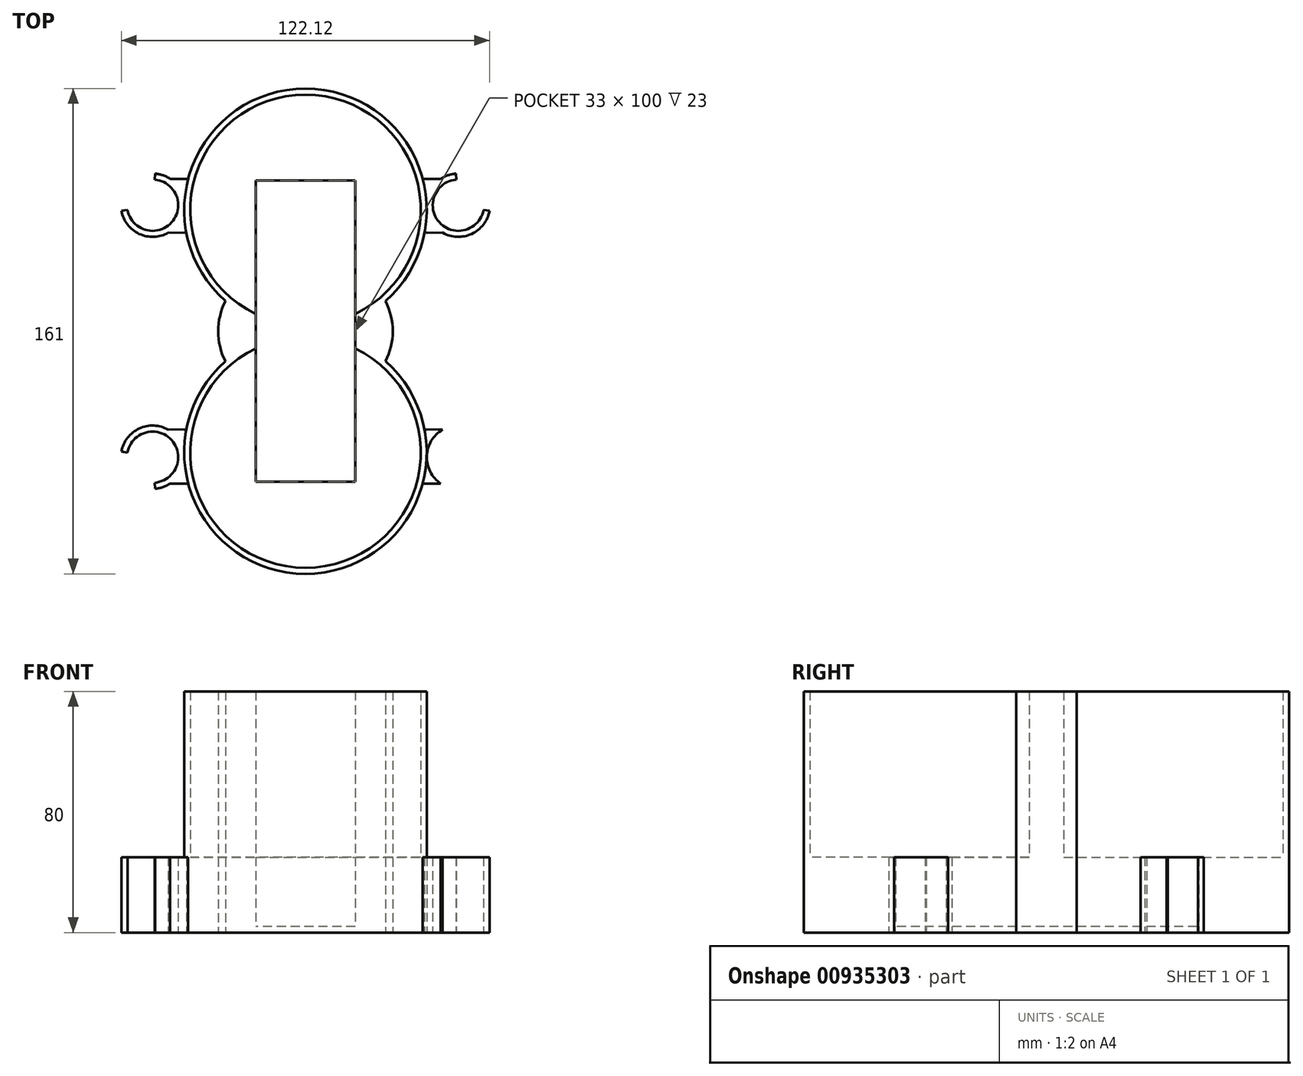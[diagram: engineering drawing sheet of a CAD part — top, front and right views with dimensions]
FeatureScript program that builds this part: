
annotation { "Feature Type Name" : "Feature", "Feature Type Description" : "" }
export const myFeature = defineFeature(function(context is Context, id is Id, definition is map)
    precondition{}
    {
        {
            var Q0;
            Q0=qCreatedBy(makeId("Top.planeOp"),FACE);
            var sketch = newSketch(context, id + "F0", { "sketchPlane" : qUnion([Q0])});
            skCircle(sketch, "E0", {"center": v(0, 40.25) * mm, "radius": 38.25 * mm});
            skCircle(sketch, "E1.0", {"center": v(0, 40.25) * mm, "radius": 40.25 * mm});
            skCircle(sketch, "E2", {"center": v(0, -40.25) * mm, "radius": 38.25 * mm});
            skCircle(sketch, "E3.0", {"center": v(0, -40.25) * mm, "radius": 40.25 * mm});
            skLineSegment(sketch, "E4", {"start": v(0, 0) * mm, "end": v(0, 0) * mm});
            skLineSegment(sketch, "E5", {"start": v(19.43, 5) * mm, "end": v(19.43, -5) * mm});
            skLineSegment(sketch, "E6.bottom", {"start": v(16.5, 50) * mm, "end": v(-16.5, 50) * mm});
            skLineSegment(sketch, "E6.top", {"start": v(16.5, -50) * mm, "end": v(-16.5, -50) * mm});
            skLineSegment(sketch, "E6.left", {"start": v(16.5, 50) * mm, "end": v(16.5, -50) * mm});
            skLineSegment(sketch, "E6.right", {"start": v(-16.5, 50) * mm, "end": v(-16.5, -50) * mm});
            skPoint(sketch, "E6.middle", {"position": v(0, 0) * mm});
            skArc(sketch, "E7", {"start": v(26.55, -10) * mm, "mid": v(28.96, 0) * mm, "end": v(26.55, 10) * mm});
            skArc(sketch, "E8.MirrorCS", {"start": v(-26.55, -10) * mm, "mid": v(-28.96, 0) * mm, "end": v(-26.55, 10) * mm});
            skLineSegment(sketch, "E9.MirrorCS", {"start": v(-19.43, 5) * mm, "end": v(-19.43, -5) * mm});
            skSolve(sketch);
        }
        {
            var Q0;
            Q0 = qSketchRegion(id + "F0", true);
            var Q1;
            {var subQ0=sQuery(id+"F0.wireOp",EDGE,"E5");Q1=makeQuery(id+"F0.imprint","IMPRINT",FACE,{"disambiguationData":[TD([[makeQuery(id+"F0.imprint","IMPRINT",EDGE,{"derivedFrom":subQ0}),-1.0]])]});}
            var Q2;
            {var subQ0=sQuery(id+"F0.wireOp",EDGE,"E9.MirrorCS");Q2=makeQuery(id+"F0.imprint","IMPRINT",FACE,{"disambiguationData":[TD([[makeQuery(id+"F0.imprint","IMPRINT",EDGE,{"derivedFrom":subQ0}),1.0]])]});}
            extrude(context, id + "F1", {"entities" : qUnion([Q0, Q1, Q2]), "depth" : 80 * mm, "offsetDistance" : 25 * mm});
        }
        {
            var Q0;
            {var subQ5=sQuery(id+"F0.wireOp",EDGE,"E6.top");Q0=makeQuery(id+"F0.imprint","IMPRINT",FACE,{"disambiguationData":[TD([[makeQuery(id+"F0.imprint","IMPRINT",EDGE,{"derivedFrom":subQ5}),1.0]])]});}
            var Q1;
            {var subQ5=sQuery(id+"F0.wireOp",EDGE,"E6.bottom");Q1=makeQuery(id+"F0.imprint","IMPRINT",FACE,{"disambiguationData":[TD([[makeQuery(id+"F0.imprint","IMPRINT",EDGE,{"derivedFrom":subQ5}),-1.0]])]});}
            var Q2;
            {var subQ5=sQuery(id+"F0.wireOp",EDGE,"E6.top");Q2=makeQuery(id+"F0.imprint","IMPRINT",FACE,{"disambiguationData":[TD([[makeQuery(id+"F0.imprint","IMPRINT",EDGE,{"derivedFrom":subQ5}),-1.0]])]});}
            var Q3;
            {var subQ5=sQuery(id+"F0.wireOp",EDGE,"E6.bottom");Q3=makeQuery(id+"F0.imprint","IMPRINT",FACE,{"disambiguationData":[TD([[makeQuery(id+"F0.imprint","IMPRINT",EDGE,{"derivedFrom":subQ5}),1.0]])]});}
            var Q4;
            {var subQ0=sQuery(id+"F0.wireOp",EDGE,"E5");Q4=makeQuery(id+"F0.imprint","IMPRINT",FACE,{"disambiguationData":[TD([[makeQuery(id+"F0.imprint","IMPRINT",EDGE,{"derivedFrom":subQ0}),-1.0]])]});}
            var Q5;
            {var subQ0=sQuery(id+"F0.wireOp",EDGE,"E9.MirrorCS");Q5=makeQuery(id+"F0.imprint","IMPRINT",FACE,{"disambiguationData":[TD([[makeQuery(id+"F0.imprint","IMPRINT",EDGE,{"derivedFrom":subQ0}),1.0]])]});}
            var Q6;
            {var subQ0=sQuery(id+"F0.wireOp",EDGE,"E6.right");var subQ1=sQuery(id+"F0.wireOp",EDGE,"E1.0");var subQ2=makeQuery(id+"F0.imprint","INTERSECT",VERTEX,{"derivedFrom":[subQ1,subQ0]});Q6=makeQuery(id+"F0.imprint","IMPRINT",FACE,{"disambiguationData":[TD([[makeQuery(id+"F0.imprint","IMPRINT",EDGE,{"disambiguationData":[TD([[subQ2,-1.0]])],"derivedFrom":subQ1}),-1.0]])]});}
            var Q7;
            {var subQ0=sQuery(id+"F0.wireOp",EDGE,"E6.left");var subQ1=sQuery(id+"F0.wireOp",EDGE,"E0");var subQ2=makeQuery(id+"F0.imprint","INTERSECT",VERTEX,{"derivedFrom":[subQ1,subQ0]});Q7=makeQuery(id+"F0.imprint","IMPRINT",FACE,{"disambiguationData":[TD([[makeQuery(id+"F0.imprint","IMPRINT",EDGE,{"disambiguationData":[TD([[subQ2,1.0]])],"derivedFrom":subQ1}),-1.0]])]});}
            var Q8;
            {var subQ2=sQuery(id+"F0.wireOp",EDGE,"E6.left");var subQ4=sQuery(id+"F0.wireOp",EDGE,"E2");var subQ5=makeQuery(id+"F0.imprint","INTERSECT",VERTEX,{"derivedFrom":[subQ4,subQ2]});Q8=makeQuery(id+"F0.imprint","IMPRINT",FACE,{"disambiguationData":[TD([[makeQuery(id+"F0.imprint","IMPRINT",EDGE,{"disambiguationData":[TD([[subQ5,-1.0]])],"derivedFrom":subQ4}),-1.0]])]});}
            var Q9;
            {var subQ0=sQuery(id+"F0.wireOp",EDGE,"E3.0");var subQ1=sQuery(id+"F0.wireOp",EDGE,"E1.0");var subQ2=makeQuery(id+"F0.imprint","INTERSECT",VERTEX,{"derivedFrom":[subQ1,subQ0]});Q9=makeQuery(id+"F0.imprint","IMPRINT",FACE,{"disambiguationData":[TD([[makeQuery(id+"F0.imprint","IMPRINT",EDGE,{"disambiguationData":[TD([[subQ2,-1.0]])],"derivedFrom":subQ1}),-1.0]])]});}
            extrude(context, id + "F2", {"entities" : qUnion([Q0, Q1, Q2, Q3, Q4, Q5, Q6, Q7, Q8, Q9]), "operationType" : NewBodyOperationType.ADD, "depth" : 25 * mm, "offsetDistance" : 25 * mm});
        }
        {
            var Q0;
            {var subQ5=sQuery(id+"F0.wireOp",EDGE,"E6.bottom");Q0=makeQuery(id+"F0.imprint","IMPRINT",FACE,{"disambiguationData":[TD([[makeQuery(id+"F0.imprint","IMPRINT",EDGE,{"derivedFrom":subQ5}),1.0]])]});}
            var Q1;
            {var subQ5=sQuery(id+"F0.wireOp",EDGE,"E6.top");Q1=makeQuery(id+"F0.imprint","IMPRINT",FACE,{"disambiguationData":[TD([[makeQuery(id+"F0.imprint","IMPRINT",EDGE,{"derivedFrom":subQ5}),-1.0]])]});}
            var Q2;
            {var subQ0=sQuery(id+"F0.wireOp",EDGE,"E6.left");var subQ1=sQuery(id+"F0.wireOp",EDGE,"E0");var subQ2=makeQuery(id+"F0.imprint","INTERSECT",VERTEX,{"derivedFrom":[subQ1,subQ0]});Q2=makeQuery(id+"F0.imprint","IMPRINT",FACE,{"disambiguationData":[TD([[makeQuery(id+"F0.imprint","IMPRINT",EDGE,{"disambiguationData":[TD([[subQ2,1.0]])],"derivedFrom":subQ1}),-1.0]])]});}
            var Q3;
            {var subQ2=sQuery(id+"F0.wireOp",EDGE,"E6.left");var subQ4=sQuery(id+"F0.wireOp",EDGE,"E2");var subQ5=makeQuery(id+"F0.imprint","INTERSECT",VERTEX,{"derivedFrom":[subQ4,subQ2]});Q3=makeQuery(id+"F0.imprint","IMPRINT",FACE,{"disambiguationData":[TD([[makeQuery(id+"F0.imprint","IMPRINT",EDGE,{"disambiguationData":[TD([[subQ5,-1.0]])],"derivedFrom":subQ4}),-1.0]])]});}
            var Q4;
            {var subQ0=sQuery(id+"F0.wireOp",EDGE,"E3.0");var subQ1=sQuery(id+"F0.wireOp",EDGE,"E1.0");var subQ2=makeQuery(id+"F0.imprint","INTERSECT",VERTEX,{"derivedFrom":[subQ1,subQ0]});Q4=makeQuery(id+"F0.imprint","IMPRINT",FACE,{"disambiguationData":[TD([[makeQuery(id+"F0.imprint","IMPRINT",EDGE,{"disambiguationData":[TD([[subQ2,-1.0]])],"derivedFrom":subQ1}),-1.0]])]});}
            var Q5;
            {var subQ0=sQuery(id+"F0.wireOp",EDGE,"E6.right");var subQ1=sQuery(id+"F0.wireOp",EDGE,"E1.0");var subQ2=makeQuery(id+"F0.imprint","INTERSECT",VERTEX,{"derivedFrom":[subQ1,subQ0]});Q5=makeQuery(id+"F0.imprint","IMPRINT",FACE,{"disambiguationData":[TD([[makeQuery(id+"F0.imprint","IMPRINT",EDGE,{"disambiguationData":[TD([[subQ2,-1.0]])],"derivedFrom":subQ1}),-1.0]])]});}
            extrude(context, id + "F3", {"entities" : qUnion([Q0, Q1, Q2, Q3, Q4, Q5]), "operationType" : NewBodyOperationType.REMOVE, "depth" : 27 * mm, "offsetDistance" : 25 * mm});
        }
        {
            var Q0;
            {var subQ5=sQuery(id+"F0.wireOp",EDGE,"E6.top");Q0=makeQuery(id+"F0.imprint","IMPRINT",FACE,{"disambiguationData":[TD([[makeQuery(id+"F0.imprint","IMPRINT",EDGE,{"derivedFrom":subQ5}),-1.0]])]});}
            var Q1;
            {var subQ0=sQuery(id+"F0.wireOp",EDGE,"E3.0");var subQ1=sQuery(id+"F0.wireOp",EDGE,"E1.0");var subQ2=makeQuery(id+"F0.imprint","INTERSECT",VERTEX,{"derivedFrom":[subQ1,subQ0]});Q1=makeQuery(id+"F0.imprint","IMPRINT",FACE,{"disambiguationData":[TD([[makeQuery(id+"F0.imprint","IMPRINT",EDGE,{"disambiguationData":[TD([[subQ2,-1.0]])],"derivedFrom":subQ1}),-1.0]])]});}
            var Q2;
            {var subQ0=sQuery(id+"F0.wireOp",EDGE,"E6.left");var subQ1=sQuery(id+"F0.wireOp",EDGE,"E2");var subQ2=makeQuery(id+"F0.imprint","INTERSECT",VERTEX,{"derivedFrom":[subQ1,subQ0]});Q2=makeQuery(id+"F0.imprint","IMPRINT",FACE,{"disambiguationData":[TD([[makeQuery(id+"F0.imprint","IMPRINT",EDGE,{"disambiguationData":[TD([[subQ2,-1.0]])],"derivedFrom":subQ1}),-1.0]])]});}
            var Q3;
            {var subQ0=sQuery(id+"F0.wireOp",EDGE,"Eti7iCEB-p9Wg-4gcS-I4jT-uz9siLTtTQbE");Q3=makeQuery(id+"F0.imprint","IMPRINT",FACE,{"disambiguationData":[TD([[makeQuery(id+"F0.imprint","IMPRINT",EDGE,{"derivedFrom":subQ0}),1.0]])]});}
            var Q4;
            {var subQ5=sQuery(id+"F0.wireOp",EDGE,"E6.bottom");Q4=makeQuery(id+"F0.imprint","IMPRINT",FACE,{"disambiguationData":[TD([[makeQuery(id+"F0.imprint","IMPRINT",EDGE,{"derivedFrom":subQ5}),1.0]])]});}
            var Q5;
            {var subQ0=sQuery(id+"F0.wireOp",EDGE,"E6.right");var subQ1=sQuery(id+"F0.wireOp",EDGE,"E1.0");var subQ2=makeQuery(id+"F0.imprint","INTERSECT",VERTEX,{"derivedFrom":[subQ1,subQ0]});Q5=makeQuery(id+"F0.imprint","IMPRINT",FACE,{"disambiguationData":[TD([[makeQuery(id+"F0.imprint","IMPRINT",EDGE,{"disambiguationData":[TD([[subQ2,-1.0]])],"derivedFrom":subQ1}),-1.0]])]});}
            var Q6;
            {var subQ0=sQuery(id+"F0.wireOp",EDGE,"E6.left");var subQ1=sQuery(id+"F0.wireOp",EDGE,"E0");var subQ2=makeQuery(id+"F0.imprint","INTERSECT",VERTEX,{"derivedFrom":[subQ1,subQ0]});Q6=makeQuery(id+"F0.imprint","IMPRINT",FACE,{"disambiguationData":[TD([[makeQuery(id+"F0.imprint","IMPRINT",EDGE,{"disambiguationData":[TD([[subQ2,1.0]])],"derivedFrom":subQ1}),-1.0]])]});}
            var Q7;
            {var subQ0=sQuery(id+"F0.wireOp",EDGE,"E5");Q7=makeQuery(id+"F0.imprint","IMPRINT",FACE,{"disambiguationData":[TD([[makeQuery(id+"F0.imprint","IMPRINT",EDGE,{"derivedFrom":subQ0}),-1.0]])]});}
            extrude(context, id + "F4", {"entities" : qUnion([Q0, Q1, Q2, Q3, Q4, Q5, Q6, Q7]), "operationType" : NewBodyOperationType.ADD, "depth" : 2 * mm, "offsetDistance" : 25 * mm});
        }
        {
            var Q0;
            Q0=qCreatedBy(makeId("Top.planeOp"),FACE);
            var sketch = newSketch(context, id + "F5", { "sketchPlane" : qUnion([Q0])});
            skArc(sketch, "E10", {"start": v(49.9, 52.27) * mm, "mid": v(42.93, 34.77) * mm, "end": v(61.06, 39.92) * mm});
            skArc(sketch, "E11.MirrorCS", {"start": v(49.9, -52.27) * mm, "mid": v(42.93, -34.77) * mm, "end": v(61.06, -39.92) * mm});
            skArc(sketch, "E12.MirrorCS", {"start": v(-49.9, 52.27) * mm, "mid": v(-42.93, 34.77) * mm, "end": v(-61.06, 39.92) * mm});
            skArc(sketch, "E13.MirrorCS", {"start": v(-49.9, -52.27) * mm, "mid": v(-42.93, -34.77) * mm, "end": v(-61.06, -39.92) * mm});
            skLineSegment(sketch, "E14", {"start": v(-44.91, 50.55) * mm, "end": v(-38.91, 50.55) * mm});
            skLineSegment(sketch, "E15", {"start": v(-45.52, 32.69) * mm, "end": v(-39.52, 32.6) * mm});
            skLineSegment(sketch, "E16.MirrorCS", {"start": v(44.91, 50.55) * mm, "end": v(38.91, 50.55) * mm});
            skLineSegment(sketch, "E17.MirrorCS", {"start": v(45.52, 32.69) * mm, "end": v(39.52, 32.6) * mm});
            skLineSegment(sketch, "E18.MirrorCS", {"start": v(-45.52, -32.69) * mm, "end": v(-39.52, -32.6) * mm});
            skLineSegment(sketch, "E19.MirrorCS", {"start": v(-44.91, -50.55) * mm, "end": v(-38.91, -50.55) * mm});
            skLineSegment(sketch, "E20.MirrorCS", {"start": v(45.52, -32.69) * mm, "end": v(39.52, -32.6) * mm});
            skLineSegment(sketch, "E21.MirrorCS", {"start": v(44.91, -50.55) * mm, "end": v(38.91, -50.55) * mm});
            skCircle(sketch, "E22.0", {"center": v(0, -40.25) * mm, "radius": 40.25 * mm});
            skCircle(sketch, "E23.0", {"center": v(0, 40.25) * mm, "radius": 40.25 * mm});
            skArc(sketch, "E24.0", {"start": v(50.06, 50.28) * mm, "mid": v(44.42, 36.1) * mm, "end": v(59.09, 40.28) * mm});
            skLineSegment(sketch, "E25", {"start": v(-49.9, 52.27) * mm, "end": v(-50.05, 50.28) * mm});
            skLineSegment(sketch, "E26", {"start": v(-50.05, -50.28) * mm, "end": v(-49.9, -52.27) * mm});
            skLineSegment(sketch, "E27", {"start": v(59.09, 40.28) * mm, "end": v(61.06, 39.92) * mm});
            skLineSegment(sketch, "E28", {"start": v(49.9, 52.27) * mm, "end": v(50.06, 50.28) * mm});
            skLineSegment(sketch, "E29.MirrorCS", {"start": v(-59.09, 40.28) * mm, "end": v(-61.06, 39.92) * mm});
            skArc(sketch, "E30.MirrorCS", {"start": v(-50.06, 50.28) * mm, "mid": v(-44.42, 36.1) * mm, "end": v(-59.09, 40.28) * mm});
            skArc(sketch, "E31.MirrorCS", {"start": v(-50.06, -50.28) * mm, "mid": v(-44.42, -36.1) * mm, "end": v(-59.09, -40.28) * mm});
            skLineSegment(sketch, "E32.MirrorCS", {"start": v(-59.09, -40.28) * mm, "end": v(-61.06, -39.92) * mm});
            skArc(sketch, "E33.MirrorCS", {"start": v(50.06, -50.28) * mm, "mid": v(44.42, -36.1) * mm, "end": v(59.09, -40.28) * mm});
            skLineSegment(sketch, "E34.MirrorCS", {"start": v(49.9, -52.27) * mm, "end": v(50.06, -50.28) * mm});
            skLineSegment(sketch, "E35.MirrorCS", {"start": v(59.09, -40.28) * mm, "end": v(61.06, -39.92) * mm});
            skSolve(sketch);
        }
        {
            var Q0;
            Q0=makeQuery(id+"F5.imprint","IMPRINT",FACE,{"disambiguationData":[TD([[makeQuery(id+"F5.imprint","IMPRINT",EDGE,{"derivedFrom":sQuery(id+"F5.wireOp",EDGE,"E24.0")}),-1.0]])]});
            var Q1;
            {var subQ0=sQuery(id+"F5.wireOp",EDGE,"E17.MirrorCS");Q1=makeQuery(id+"F5.imprint","IMPRINT",FACE,{"disambiguationData":[TD([[makeQuery(id+"F5.imprint","IMPRINT",EDGE,{"derivedFrom":subQ0}),-1.0]])]});}
            var Q2;
            {var subQ0=sQuery(id+"F5.wireOp",EDGE,"E16.MirrorCS");Q2=makeQuery(id+"F5.imprint","IMPRINT",FACE,{"disambiguationData":[TD([[makeQuery(id+"F5.imprint","IMPRINT",EDGE,{"derivedFrom":subQ0}),1.0]])]});}
            var Q3;
            {var subQ4=sQuery(id+"F5.wireOp",EDGE,"E25");Q3=makeQuery(id+"F5.imprint","IMPRINT",FACE,{"disambiguationData":[TD([[makeQuery(id+"F5.imprint","IMPRINT",EDGE,{"derivedFrom":subQ4}),1.0]])]});}
            var Q4;
            {var subQ0=sQuery(id+"F5.wireOp",EDGE,"E15");Q4=makeQuery(id+"F5.imprint","IMPRINT",FACE,{"disambiguationData":[TD([[makeQuery(id+"F5.imprint","IMPRINT",EDGE,{"derivedFrom":subQ0}),1.0]])]});}
            var Q5;
            {var subQ0=sQuery(id+"F5.wireOp",EDGE,"E14");Q5=makeQuery(id+"F5.imprint","IMPRINT",FACE,{"disambiguationData":[TD([[makeQuery(id+"F5.imprint","IMPRINT",EDGE,{"derivedFrom":subQ0}),-1.0]])]});}
            var Q6;
            Q6=makeQuery(id+"F5.imprint","IMPRINT",FACE,{"disambiguationData":[TD([[makeQuery(id+"F5.imprint","IMPRINT",EDGE,{"derivedFrom":sQuery(id+"F5.wireOp",EDGE,"E33.MirrorCS")}),1.0]])]});
            var Q7;
            {var subQ0=sQuery(id+"F5.wireOp",EDGE,"E20.MirrorCS");Q7=makeQuery(id+"F5.imprint","IMPRINT",FACE,{"disambiguationData":[TD([[makeQuery(id+"F5.imprint","IMPRINT",EDGE,{"derivedFrom":subQ0}),1.0]])]});}
            var Q8;
            {var subQ0=sQuery(id+"F5.wireOp",EDGE,"E21.MirrorCS");Q8=makeQuery(id+"F5.imprint","IMPRINT",FACE,{"disambiguationData":[TD([[makeQuery(id+"F5.imprint","IMPRINT",EDGE,{"derivedFrom":subQ0}),-1.0]])]});}
            var Q9;
            {var subQ0=sQuery(id+"F5.wireOp",EDGE,"E18.MirrorCS");Q9=makeQuery(id+"F5.imprint","IMPRINT",FACE,{"disambiguationData":[TD([[makeQuery(id+"F5.imprint","IMPRINT",EDGE,{"derivedFrom":subQ0}),-1.0]])]});}
            var Q10;
            {var subQ0=sQuery(id+"F5.wireOp",EDGE,"E19.MirrorCS");Q10=makeQuery(id+"F5.imprint","IMPRINT",FACE,{"disambiguationData":[TD([[makeQuery(id+"F5.imprint","IMPRINT",EDGE,{"derivedFrom":subQ0}),1.0]])]});}
            var Q11;
            {var subQ4=sQuery(id+"F5.wireOp",EDGE,"E26");Q11=makeQuery(id+"F5.imprint","IMPRINT",FACE,{"disambiguationData":[TD([[makeQuery(id+"F5.imprint","IMPRINT",EDGE,{"derivedFrom":subQ4}),1.0]])]});}
            extrude(context, id + "F6", {"entities" : qUnion([Q0, Q1, Q2, Q3, Q4, Q5, Q6, Q7, Q8, Q9, Q10, Q11]), "operationType" : NewBodyOperationType.ADD, "depth" : 25 * mm, "offsetDistance" : 25 * mm});
        }
    });
